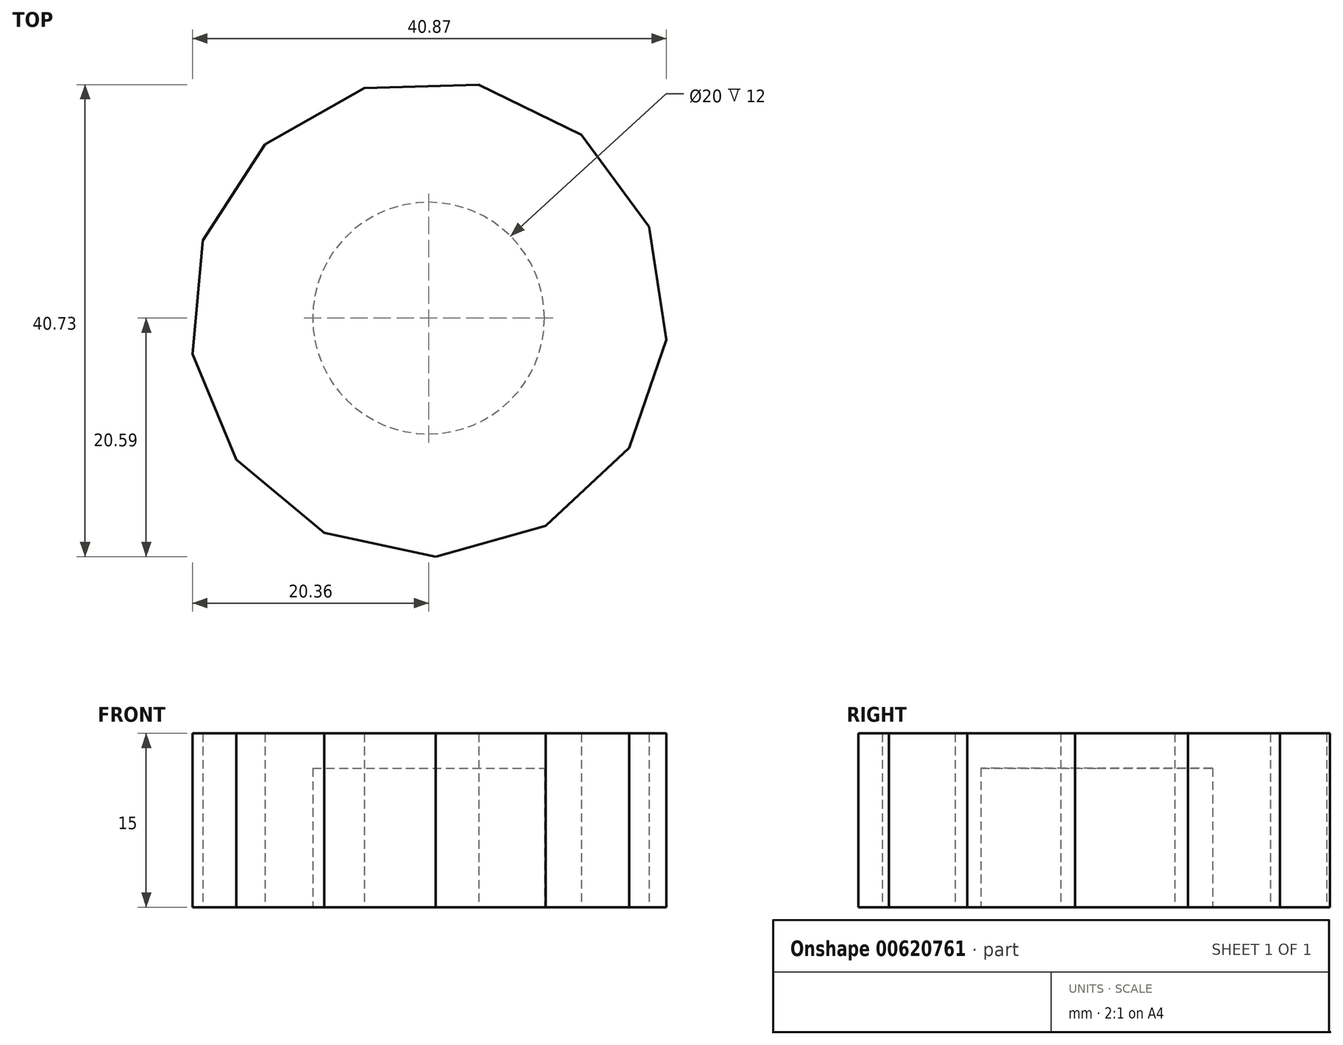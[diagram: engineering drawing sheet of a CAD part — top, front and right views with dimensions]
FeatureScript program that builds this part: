
annotation { "Feature Type Name" : "Feature", "Feature Type Description" : "" }
export const myFeature = defineFeature(function(context is Context, id is Id, definition is map)
    precondition{}
    {
        {
            var Q0;
            Q0=qCreatedBy(makeId("Top.planeOp"),FACE);
            var sketch = newSketch(context, id + "F0", { "sketchPlane" : qUnion([Q0])});
            skCircle(sketch, "E0", {"center": v(0, 0) * mm, "radius": 20 * mm});
            skLineSegment(sketch, "E1.0", {"start": v(-16.59, -12.21) * mm, "end": v(-20.36, -3.1) * mm});
            skLineSegment(sketch, "E1.1", {"start": v(-20.36, -3.1) * mm, "end": v(-19.47, 6.72) * mm});
            skLineSegment(sketch, "E1.2", {"start": v(-19.47, 6.72) * mm, "end": v(-14.12, 15) * mm});
            skLineSegment(sketch, "E1.3", {"start": v(-14.12, 15) * mm, "end": v(-5.54, 19.84) * mm});
            skLineSegment(sketch, "E1.4", {"start": v(-5.54, 19.84) * mm, "end": v(4.32, 20.14) * mm});
            skLineSegment(sketch, "E1.5", {"start": v(4.32, 20.14) * mm, "end": v(13.18, 15.83) * mm});
            skLineSegment(sketch, "E1.6", {"start": v(13.18, 15.83) * mm, "end": v(19.03, 7.89) * mm});
            skLineSegment(sketch, "E1.7", {"start": v(19.03, 7.89) * mm, "end": v(20.51, -1.86) * mm});
            skLineSegment(sketch, "E1.8", {"start": v(20.51, -1.86) * mm, "end": v(17.3, -11.18) * mm});
            skLineSegment(sketch, "E1.9", {"start": v(17.3, -11.18) * mm, "end": v(10.12, -17.94) * mm});
            skLineSegment(sketch, "E1.10", {"start": v(10.12, -17.94) * mm, "end": v(0.63, -20.59) * mm});
            skLineSegment(sketch, "E1.11", {"start": v(0.63, -20.59) * mm, "end": v(-9.01, -18.52) * mm});
            skLineSegment(sketch, "E1.12", {"start": v(-9.01, -18.52) * mm, "end": v(-16.59, -12.21) * mm});
            skPoint(sketch, "E1.0.midPoint", {"position": v(-18.48, -7.66) * mm});
            skSolve(sketch);
        }
        {
            var Q0;
            {var subQ0=sQuery(id+"F0.wireOp",EDGE,"E1.7");var subQ1=sQuery(id+"F0.wireOp",EDGE,"E0");var subQ2=makeQuery(id+"F0.imprint","INTERSECT",VERTEX,{"derivedFrom":[subQ1,subQ0]});Q0=makeQuery(id+"F0.imprint","IMPRINT",FACE,{"disambiguationData":[TD([[makeQuery(id+"F0.imprint","IMPRINT",EDGE,{"disambiguationData":[TD([[subQ2,1.0]])],"derivedFrom":subQ1}),-1.0]])]});}
            var Q1;
            {var subQ0=sQuery(id+"F0.wireOp",EDGE,"E1.9");var subQ1=sQuery(id+"F0.wireOp",EDGE,"E0");var subQ2=makeQuery(id+"F0.imprint","INTERSECT",VERTEX,{"derivedFrom":[subQ1,subQ0]});Q1=makeQuery(id+"F0.imprint","IMPRINT",FACE,{"disambiguationData":[TD([[makeQuery(id+"F0.imprint","IMPRINT",EDGE,{"disambiguationData":[TD([[subQ2,-1.0]])],"derivedFrom":subQ1}),-1.0]])]});}
            var Q2;
            {var subQ0=sQuery(id+"F0.wireOp",EDGE,"E1.10");var subQ1=sQuery(id+"F0.wireOp",EDGE,"E0");var subQ2=makeQuery(id+"F0.imprint","INTERSECT",VERTEX,{"derivedFrom":[subQ1,subQ0]});Q2=makeQuery(id+"F0.imprint","IMPRINT",FACE,{"disambiguationData":[TD([[makeQuery(id+"F0.imprint","IMPRINT",EDGE,{"disambiguationData":[TD([[subQ2,-1.0]])],"derivedFrom":subQ1}),-1.0]])]});}
            var Q3;
            {var subQ0=sQuery(id+"F0.wireOp",EDGE,"E1.11");var subQ1=sQuery(id+"F0.wireOp",EDGE,"E0");var subQ2=makeQuery(id+"F0.imprint","INTERSECT",VERTEX,{"derivedFrom":[subQ1,subQ0]});Q3=makeQuery(id+"F0.imprint","IMPRINT",FACE,{"disambiguationData":[TD([[makeQuery(id+"F0.imprint","IMPRINT",EDGE,{"disambiguationData":[TD([[subQ2,-1.0]])],"derivedFrom":subQ1}),-1.0]])]});}
            var Q4;
            {var subQ0=sQuery(id+"F0.wireOp",EDGE,"E1.12");var subQ1=sQuery(id+"F0.wireOp",EDGE,"E0");var subQ2=makeQuery(id+"F0.imprint","INTERSECT",VERTEX,{"derivedFrom":[subQ1,subQ0]});Q4=makeQuery(id+"F0.imprint","IMPRINT",FACE,{"disambiguationData":[TD([[makeQuery(id+"F0.imprint","IMPRINT",EDGE,{"disambiguationData":[TD([[subQ2,-1.0]])],"derivedFrom":subQ1}),-1.0]])]});}
            var Q5;
            {var subQ0=sQuery(id+"F0.wireOp",EDGE,"E1.0");var subQ1=sQuery(id+"F0.wireOp",EDGE,"E0");var subQ2=makeQuery(id+"F0.imprint","INTERSECT",VERTEX,{"derivedFrom":[subQ1,subQ0]});Q5=makeQuery(id+"F0.imprint","IMPRINT",FACE,{"disambiguationData":[TD([[makeQuery(id+"F0.imprint","IMPRINT",EDGE,{"disambiguationData":[TD([[subQ2,-1.0]])],"derivedFrom":subQ1}),-1.0]])]});}
            var Q6;
            {var subQ0=sQuery(id+"F0.wireOp",EDGE,"E1.1");var subQ1=sQuery(id+"F0.wireOp",EDGE,"E0");var subQ2=makeQuery(id+"F0.imprint","INTERSECT",VERTEX,{"derivedFrom":[subQ1,subQ0]});Q6=makeQuery(id+"F0.imprint","IMPRINT",FACE,{"disambiguationData":[TD([[makeQuery(id+"F0.imprint","IMPRINT",EDGE,{"disambiguationData":[TD([[subQ2,-1.0]])],"derivedFrom":subQ1}),-1.0]])]});}
            var Q7;
            {var subQ0=sQuery(id+"F0.wireOp",EDGE,"E1.2");var subQ1=sQuery(id+"F0.wireOp",EDGE,"E0");var subQ2=makeQuery(id+"F0.imprint","INTERSECT",VERTEX,{"derivedFrom":[subQ1,subQ0]});Q7=makeQuery(id+"F0.imprint","IMPRINT",FACE,{"disambiguationData":[TD([[makeQuery(id+"F0.imprint","IMPRINT",EDGE,{"disambiguationData":[TD([[subQ2,-1.0]])],"derivedFrom":subQ1}),-1.0]])]});}
            var Q8;
            {var subQ0=sQuery(id+"F0.wireOp",EDGE,"E1.3");var subQ1=sQuery(id+"F0.wireOp",EDGE,"E0");var subQ2=makeQuery(id+"F0.imprint","INTERSECT",VERTEX,{"derivedFrom":[subQ1,subQ0]});Q8=makeQuery(id+"F0.imprint","IMPRINT",FACE,{"disambiguationData":[TD([[makeQuery(id+"F0.imprint","IMPRINT",EDGE,{"disambiguationData":[TD([[subQ2,-1.0]])],"derivedFrom":subQ1}),-1.0]])]});}
            var Q9;
            {var subQ0=sQuery(id+"F0.wireOp",EDGE,"E1.4");var subQ1=sQuery(id+"F0.wireOp",EDGE,"E0");var subQ2=makeQuery(id+"F0.imprint","INTERSECT",VERTEX,{"derivedFrom":[subQ1,subQ0]});Q9=makeQuery(id+"F0.imprint","IMPRINT",FACE,{"disambiguationData":[TD([[makeQuery(id+"F0.imprint","IMPRINT",EDGE,{"disambiguationData":[TD([[subQ2,-1.0]])],"derivedFrom":subQ1}),-1.0]])]});}
            var Q10;
            {var subQ0=sQuery(id+"F0.wireOp",EDGE,"E1.5");var subQ1=sQuery(id+"F0.wireOp",EDGE,"E0");var subQ2=makeQuery(id+"F0.imprint","INTERSECT",VERTEX,{"derivedFrom":[subQ1,subQ0]});Q10=makeQuery(id+"F0.imprint","IMPRINT",FACE,{"disambiguationData":[TD([[makeQuery(id+"F0.imprint","IMPRINT",EDGE,{"disambiguationData":[TD([[subQ2,-1.0]])],"derivedFrom":subQ1}),-1.0]])]});}
            var Q11;
            {var subQ0=sQuery(id+"F0.wireOp",EDGE,"E1.6");var subQ1=sQuery(id+"F0.wireOp",EDGE,"E0");var subQ2=makeQuery(id+"F0.imprint","INTERSECT",VERTEX,{"derivedFrom":[subQ1,subQ0]});Q11=makeQuery(id+"F0.imprint","IMPRINT",FACE,{"disambiguationData":[TD([[makeQuery(id+"F0.imprint","IMPRINT",EDGE,{"disambiguationData":[TD([[subQ2,-1.0]])],"derivedFrom":subQ1}),-1.0]])]});}
            var Q12;
            {var subQ0=sQuery(id+"F0.wireOp",EDGE,"E1.6");var subQ1=sQuery(id+"F0.wireOp",EDGE,"E0");var subQ2=makeQuery(id+"F0.imprint","INTERSECT",VERTEX,{"derivedFrom":[subQ1,subQ0]});Q12=makeQuery(id+"F0.imprint","IMPRINT",FACE,{"disambiguationData":[TD([[makeQuery(id+"F0.imprint","IMPRINT",EDGE,{"disambiguationData":[TD([[subQ2,1.0]])],"derivedFrom":subQ1}),-1.0]])]});}
            var Q13;
            {var subQ0=sQuery(id+"F0.wireOp",EDGE,"E0");var subQ8=makeQuery(id+"F0.imprint","INTERSECT",VERTEX,{"derivedFrom":[subQ0,sQuery(id+"F0.wireOp",EDGE,"E1.6")]});Q13=makeQuery(id+"F0.imprint","IMPRINT",FACE,{"disambiguationData":[TD([[makeQuery(id+"F0.imprint","IMPRINT",EDGE,{"disambiguationData":[TD([[subQ8,1.0]])],"derivedFrom":subQ0}),1.0]])]});}
            extrude(context, id + "F1", {"entities" : qUnion([Q0, Q1, Q2, Q3, Q4, Q5, Q6, Q7, Q8, Q9, Q10, Q11, Q12, Q13]), "depth" : 15 * mm, "offsetDistance" : 25 * mm});
        }
        {
            var Q0;
            Q0=makeQuery(id+"F1.opExtrude","CAP_FACE",FACE,{"disambiguationData":[OSD([sQuery(id+"F0.wireOp",EDGE,"E1.0"),sQuery(id+"F0.wireOp",EDGE,"E1.1"),sQuery(id+"F0.wireOp",EDGE,"E1.2"),sQuery(id+"F0.wireOp",EDGE,"E1.3"),sQuery(id+"F0.wireOp",EDGE,"E1.4"),sQuery(id+"F0.wireOp",EDGE,"E1.5"),sQuery(id+"F0.wireOp",EDGE,"E1.6"),sQuery(id+"F0.wireOp",EDGE,"E1.7"),sQuery(id+"F0.wireOp",EDGE,"E1.8"),sQuery(id+"F0.wireOp",EDGE,"E1.9"),sQuery(id+"F0.wireOp",EDGE,"E1.10"),sQuery(id+"F0.wireOp",EDGE,"E1.11"),sQuery(id+"F0.wireOp",EDGE,"E1.12")])],"isStart":true});
            var sketch = newSketch(context, id + "F2", { "sketchPlane" : qUnion([Q0])});
            skCircle(sketch, "E2", {"center": v(0, 0) * mm, "radius": 10 * mm});
            skSolve(sketch);
        }
        {
            var Q0;
            Q0 = qSketchRegion(id + "F2", true);
            extrude(context, id + "F3", {"entities" : qUnion([Q0]), "operationType" : NewBodyOperationType.REMOVE, "oppositeDirection" : true, "depth" : 12 * mm, "offsetDistance" : 25 * mm});
        }
    });
